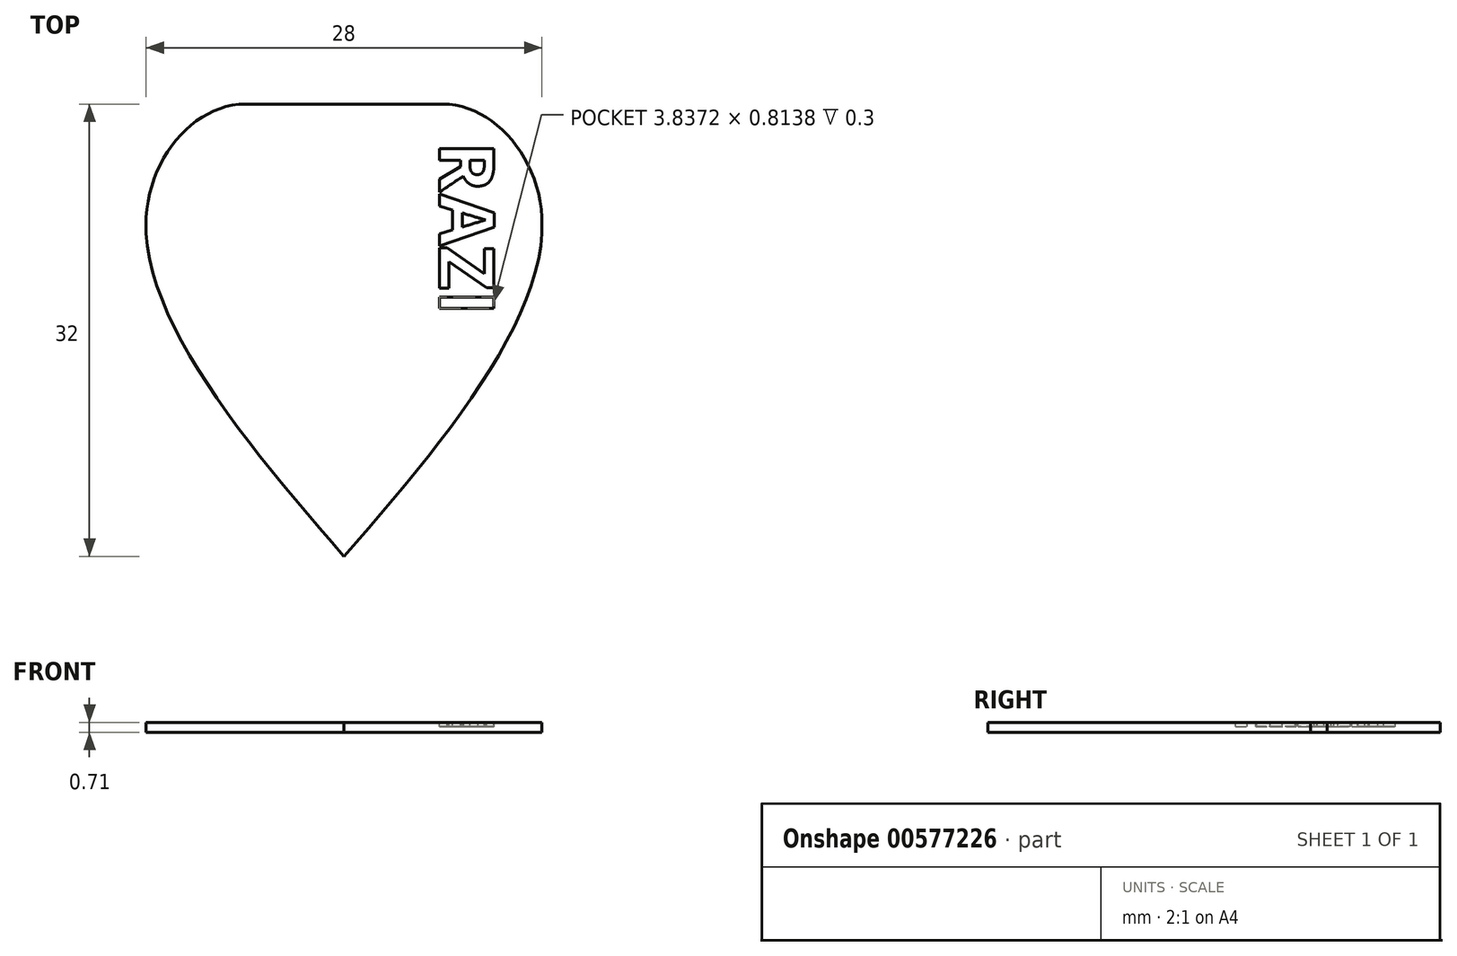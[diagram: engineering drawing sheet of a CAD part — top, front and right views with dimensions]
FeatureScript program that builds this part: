
annotation { "Feature Type Name" : "Feature", "Feature Type Description" : "" }
export const myFeature = defineFeature(function(context is Context, id is Id, definition is map)
    precondition{}
    {
        {
            var Q0;
            Q0=qCreatedBy(makeId("Top.planeOp"),FACE);
            var sketch = newSketch(context, id + "F0", { "sketchPlane" : qUnion([Q0])});
            skLineSegment(sketch, "E0.bottom", {"start": v(14, -16) * mm, "end": v(-14, -16) * mm});
            skLineSegment(sketch, "E0.top", {"start": v(14, 16) * mm, "end": v(-14, 16) * mm});
            skLineSegment(sketch, "E0.left", {"start": v(14, -16) * mm, "end": v(14, 16) * mm});
            skLineSegment(sketch, "E0.right", {"start": v(-14, -16) * mm, "end": v(-14, 16) * mm});
            skPoint(sketch, "E0.middle", {"position": v(0, 0) * mm});
            skPoint(sketch, "E1", {"position": v(-14, 0) * mm});
            skPoint(sketch, "E2", {"position": v(0, 16) * mm});
            skPoint(sketch, "E3", {"position": v(14, 0) * mm});
            skPoint(sketch, "E4", {"position": v(0, -16) * mm});
            skPoint(sketch, "E5", {"position": v(-14, 8) * mm});
            skPoint(sketch, "E6.MirrorP", {"position": v(14, 8) * mm});
            skPoint(sketch, "E7", {"position": v(7, 16) * mm});
            skPoint(sketch, "E8.MirrorP", {"position": v(-7, 16) * mm});
            skFitSpline(sketch, "E9", {"points": [v(-7, 16) * mm, v(-14, 8) * mm, v(0, -16) * mm], "startDerivative": vector(-27.48, 0) * mm, "endDerivative": vector(33.99, -38.84) * mm});
            skFitSpline(sketch, "E10", {"points": [v(7, 16) * mm, v(14, 8) * mm, v(0, -16) * mm], "startDerivative": vector(27.48, 0) * mm, "endDerivative": vector(-33.99, -38.84) * mm});
            skPoint(sketch, "E11", {"position": v(14, -8) * mm});
            skPoint(sketch, "E12", {"position": v(7, -16) * mm});
            skPoint(sketch, "E13.MirrorP", {"position": v(-14, -8) * mm});
            skPoint(sketch, "E14.MirrorP", {"position": v(-7, -16) * mm});
            skSolve(sketch);
        }
        {
            var Q0;
            {var subQ0=sQuery(id+"F0.wireOp",EDGE,"E9");var subQ4=sQuery(id+"F0.wireOp",EDGE,"E0.top");var subQ5=makeQuery(id+"F0.imprint","INTERSECT",VERTEX,{"derivedFrom":[subQ4,subQ0]});Q0=makeQuery(id+"F0.imprint","IMPRINT",FACE,{"disambiguationData":[TD([[makeQuery(id+"F0.imprint","IMPRINT",EDGE,{"disambiguationData":[TD([[subQ5,1.0]])],"derivedFrom":subQ4}),1.0]])]});}
            extrude(context, id + "F1", {"entities" : qUnion([Q0]), "depth" : 0.71 * mm, "offsetDistance" : 25 * mm});
        }
        {
            var Q0;
            Q0=makeQuery(id+"F1.opExtrude","CAP_FACE",FACE,{"disambiguationData":[OSD([sQuery(id+"F0.wireOp",EDGE,"E0.top"),sQuery(id+"F0.wireOp",EDGE,"E0.left"),sQuery(id+"F0.wireOp",EDGE,"E0.right"),sQuery(id+"F0.wireOp",EDGE,"E9"),sQuery(id+"F0.wireOp",EDGE,"E10")])],"isStart":false});
            cPlane(context, id + "F2", {"entities" : qUnion([Q0]), "cplaneType" : CPlaneType.OFFSET, "offset" : 0 * mm, "width" : 150 * mm, "height" : 150 * mm});
        }
        {
            var Q0;
            Q0=qCreatedBy(id+"F2.planeOp",FACE);
            var sketch = newSketch(context, id + "F3", { "sketchPlane" : qUnion([Q0])});
            skText(sketch, "E15", { "text": "RAZI", "fontName": "OpenSans-Bold.ttf"});
            skLineSegment(sketch, "E16", {"start": v(6.77, 9.78) * mm, "end": v(6.76, 9.78) * mm});
            const initialGuessF3  = {"E15": [0.00676, 0.01332, 0, -1, 0.00387]};
            skSetInitialGuess(sketch, initialGuessF3);
            skSolve(sketch);
        }
        {
            var Q0;
            {var subQ0=sQuery(id+"F3.wireOp",EDGE,"E15.sketch_text.stroke-44");Q0=makeQuery(id+"F3.imprint","IMPRINT",FACE,{"disambiguationData":[TD([[makeQuery(id+"F3.imprint","IMPRINT",EDGE,{"derivedFrom":subQ0}),-1.0]])]});}
            var Q1;
            {var subQ0=sQuery(id+"F3.wireOp",EDGE,"E15.sketch_text.stroke-42");Q1=makeQuery(id+"F3.imprint","IMPRINT",FACE,{"disambiguationData":[TD([[makeQuery(id+"F3.imprint","IMPRINT",EDGE,{"derivedFrom":subQ0}),-1.0]])]});}
            var Q2;
            {var subQ0=sQuery(id+"F3.wireOp",EDGE,"E15.sketch_text.stroke-40");var subQ1=sQuery(id+"F3.wireOp",EDGE,"E15.sketch_text.stroke-31");var subQ2=makeQuery(id+"F3.imprint","INTERSECT",VERTEX,{"derivedFrom":[subQ1,subQ0]});Q2=makeQuery(id+"F3.imprint","IMPRINT",FACE,{"disambiguationData":[TD([[makeQuery(id+"F3.imprint","IMPRINT",EDGE,{"disambiguationData":[TD([[subQ2,-1.0]])],"derivedFrom":subQ1}),-1.0]])]});}
            var Q3;
            {var subQ4=sQuery(id+"F3.wireOp",EDGE,"E15.sketch_text.stroke-2");Q3=makeQuery(id+"F3.imprint","IMPRINT",FACE,{"disambiguationData":[TD([[makeQuery(id+"F3.imprint","IMPRINT",EDGE,{"derivedFrom":subQ4}),-1.0]])]});}
            var Q4;
            {var subQ0=sQuery(id+"F3.wireOp",EDGE,"E16");var subQ3=sQuery(id+"F3.wireOp",EDGE,"E15.sketch_text.stroke-15");var subQ4=makeQuery(id+"F3.imprint","INTERSECT",VERTEX,{"derivedFrom":[subQ3,subQ0]});Q4=makeQuery(id+"F3.imprint","IMPRINT",FACE,{"disambiguationData":[TD([[makeQuery(id+"F3.imprint","IMPRINT",EDGE,{"disambiguationData":[TD([[subQ4,1.0]])],"derivedFrom":subQ3}),-1.0]])]});}
            var Q5;
            {var subQ0=sQuery(id+"F3.wireOp",EDGE,"E15.sketch_text.stroke-8");Q5=makeQuery(id+"F3.imprint","IMPRINT",FACE,{"disambiguationData":[TD([[makeQuery(id+"F3.imprint","IMPRINT",EDGE,{"derivedFrom":subQ0}),-1.0]])]});}
            var Q6;
            {var subQ0=sQuery(id+"F3.wireOp",EDGE,"E15.sketch_text.stroke-33");Q6=makeQuery(id+"F3.imprint","IMPRINT",FACE,{"disambiguationData":[TD([[makeQuery(id+"F3.imprint","IMPRINT",EDGE,{"derivedFrom":subQ0}),-1.0]])]});}
            var Q7;
            {var subQ0=sQuery(id+"F3.wireOp",EDGE,"E15.sketch_text.stroke-22");Q7=makeQuery(id+"F3.imprint","IMPRINT",FACE,{"disambiguationData":[TD([[makeQuery(id+"F3.imprint","IMPRINT",EDGE,{"derivedFrom":subQ0}),-1.0]])]});}
            var Q8;
            {var subQ6=sQuery(id+"F3.wireOp",EDGE,"E15.sketch_text.stroke-20");Q8=makeQuery(id+"F3.imprint","IMPRINT",FACE,{"disambiguationData":[TD([[makeQuery(id+"F3.imprint","IMPRINT",EDGE,{"derivedFrom":subQ6}),-1.0]])]});}
            extrude(context, id + "F4", {"entities" : qUnion([Q0, Q1, Q2, Q3, Q4, Q5, Q6, Q7, Q8]), "operationType" : NewBodyOperationType.REMOVE, "oppositeDirection" : true, "depth" : 0.3 * mm, "offsetDistance" : 25 * mm});
        }
    });
